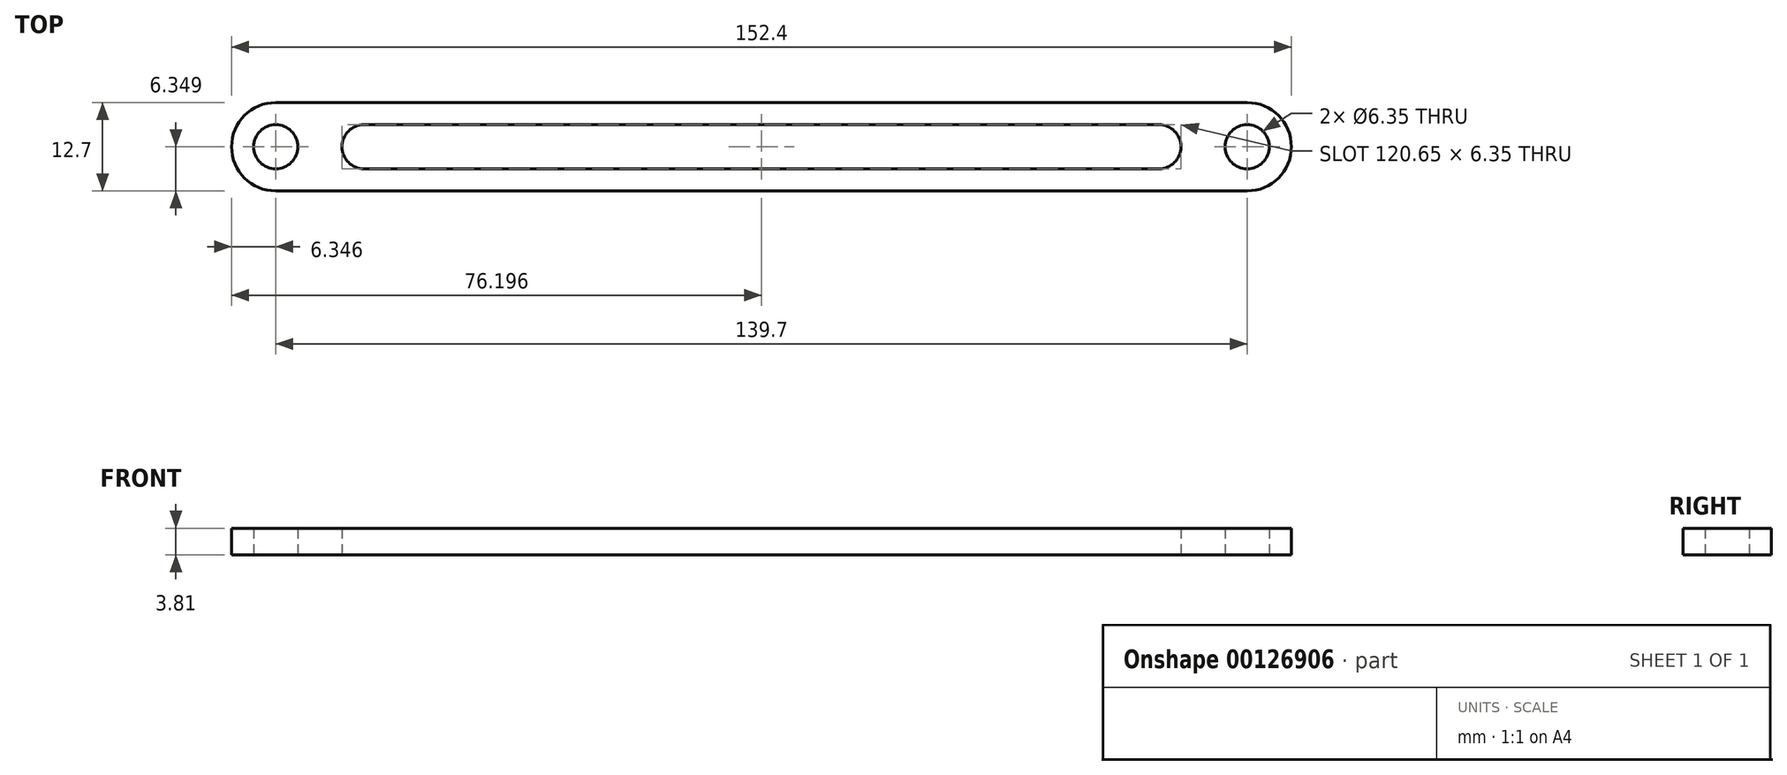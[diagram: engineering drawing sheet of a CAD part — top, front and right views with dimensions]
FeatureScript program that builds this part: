
annotation { "Feature Type Name" : "Feature", "Feature Type Description" : "" }
export const myFeature = defineFeature(function(context is Context, id is Id, definition is map)
    precondition{}
    {
        {
            var Q0;
            Q0=qCreatedBy(makeId("Top.planeOp"),FACE);
            var sketch = newSketch(context, id + "F0", { "sketchPlane" : qUnion([Q0])});
            skLineSegment(sketch, "E0.bottom", {"start": v(-64.97, 3.46) * mm, "end": v(74.73, 3.46) * mm});
            skLineSegment(sketch, "E0.top", {"start": v(-64.97, -9.24) * mm, "end": v(74.73, -9.24) * mm});
            skCircle(sketch, "E1", {"center": v(-64.97, -2.9) * mm, "radius": 6.35 * mm});
            skCircle(sketch, "E2", {"center": v(74.73, -2.9) * mm, "radius": 6.35 * mm});
            skCircle(sketch, "E3", {"center": v(-64.97, -2.9) * mm, "radius": 3.18 * mm});
            skCircle(sketch, "E4", {"center": v(74.73, -2.9) * mm, "radius": 3.18 * mm});
            skCircle(sketch, "E5", {"center": v(-52.27, -2.9) * mm, "radius": 3.18 * mm});
            skCircle(sketch, "E6", {"center": v(62.03, -2.9) * mm, "radius": 3.18 * mm});
            skLineSegment(sketch, "E7", {"start": v(-52.27, -6.07) * mm, "end": v(62.03, -6.07) * mm});
            skLineSegment(sketch, "E8", {"start": v(-52.27, 0.28) * mm, "end": v(62.03, 0.28) * mm});
            skSolve(sketch);
        }
        {
            var Q0;
            {var subQ1=sQuery(id+"F0.wireOp",EDGE,"E0.bottom");Q0=makeQuery(id+"F0.imprint","IMPRINT",FACE,{"disambiguationData":[TD([[makeQuery(id+"F0.imprint","IMPRINT",EDGE,{"derivedFrom":subQ1}),-1.0]])]});}
            var Q1;
            Q1=makeQuery(id+"F0.imprint","IMPRINT",FACE,{"disambiguationData":[TD([[makeQuery(id+"F0.imprint","IMPRINT",EDGE,{"derivedFrom":sQuery(id+"F0.wireOp",EDGE,"E4")}),-1.0]])]});
            var Q2;
            Q2=makeQuery(id+"F0.imprint","IMPRINT",FACE,{"disambiguationData":[TD([[makeQuery(id+"F0.imprint","IMPRINT",EDGE,{"derivedFrom":sQuery(id+"F0.wireOp",EDGE,"E3")}),-1.0]])]});
            extrude(context, id + "F1", {"entities" : qUnion([Q0, Q1, Q2]), "depth" : 3.8 * mm});
        }
    });
